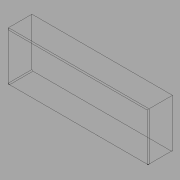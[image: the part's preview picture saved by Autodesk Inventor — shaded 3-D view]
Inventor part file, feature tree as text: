
AUTODESK INVENTOR PART (.ipt)
format: ipt  version: 2022.1 (Build 261234020, 234B)  size: 117,248 bytes
history: native  units: in
note: dims shown in document units (in); Inventor stores cm internally (conversion verified against a paired STEP export)
features: extrude x1, fillet x1, sketch x1
ambient origin geometry x8: Origin, YZ Plane, XZ Plane, XY Plane, X Axis, Y Axis, Z Axis, Center Point
bodies: Solid1 (feature_tree)
feature tree (3):
  extrude  "Extrusion1"  Depth=12.0in
  fillet  "Fillet1"  Radius=6.0in
  sketch  "Sketch1"  dims[d0=34.5in d1=12.0in d2=6.0in d3=0.0in d4=0.25in]
